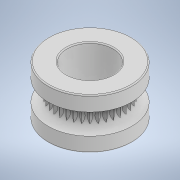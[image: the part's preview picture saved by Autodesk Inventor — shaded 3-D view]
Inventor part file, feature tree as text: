
AUTODESK INVENTOR PART (.ipt)
format: ipt  version: 2021 (Build 250183000, 183)  size: 323,584 bytes
history: native  units: in
note: dims shown in document units (in); Inventor stores cm internally (conversion verified against a paired STEP export)
features: sketch x2, revolve x1, mirror x1, fillet x1, extrude x1, pattern_circular x1
ambient origin geometry x8: Origin, YZ Plane, XZ Plane, XY Plane, X Axis, Y Axis, Z Axis, Center Point
bodies: Solid1 (feature_tree)
feature tree (7):
  revolve  "Revolution1"  [1 undecoded]
  mirror  "Mirror1"
  fillet  "Fillet1"  Radius=0.4331in
  extrude  "Extrusion1"  Depth=0.1969in
  pattern_circular  "Circular Pattern1"  Angle=90.0deg  [1 undecoded]
  sketch  "Sketch1"  dims[d0=0.7874in d1=0.4724in d2=0.4331in]
  sketch  "Sketch2"  dims[d3=0.0in d4=0.1969in d5=90.0deg d6=0.0197in d7=1.1811in d8=0.8858in d9=0.8858in d10=0.4429in d11=0.4429in d12=0.9449in d13=0.0in d14=14.1732in d15=360.0deg]
note: 2 required parameter values undecoded (feature->parameter linkage not recoverable at this tier; creation-order binding heuristic only, values carry confidence <= 0.55)